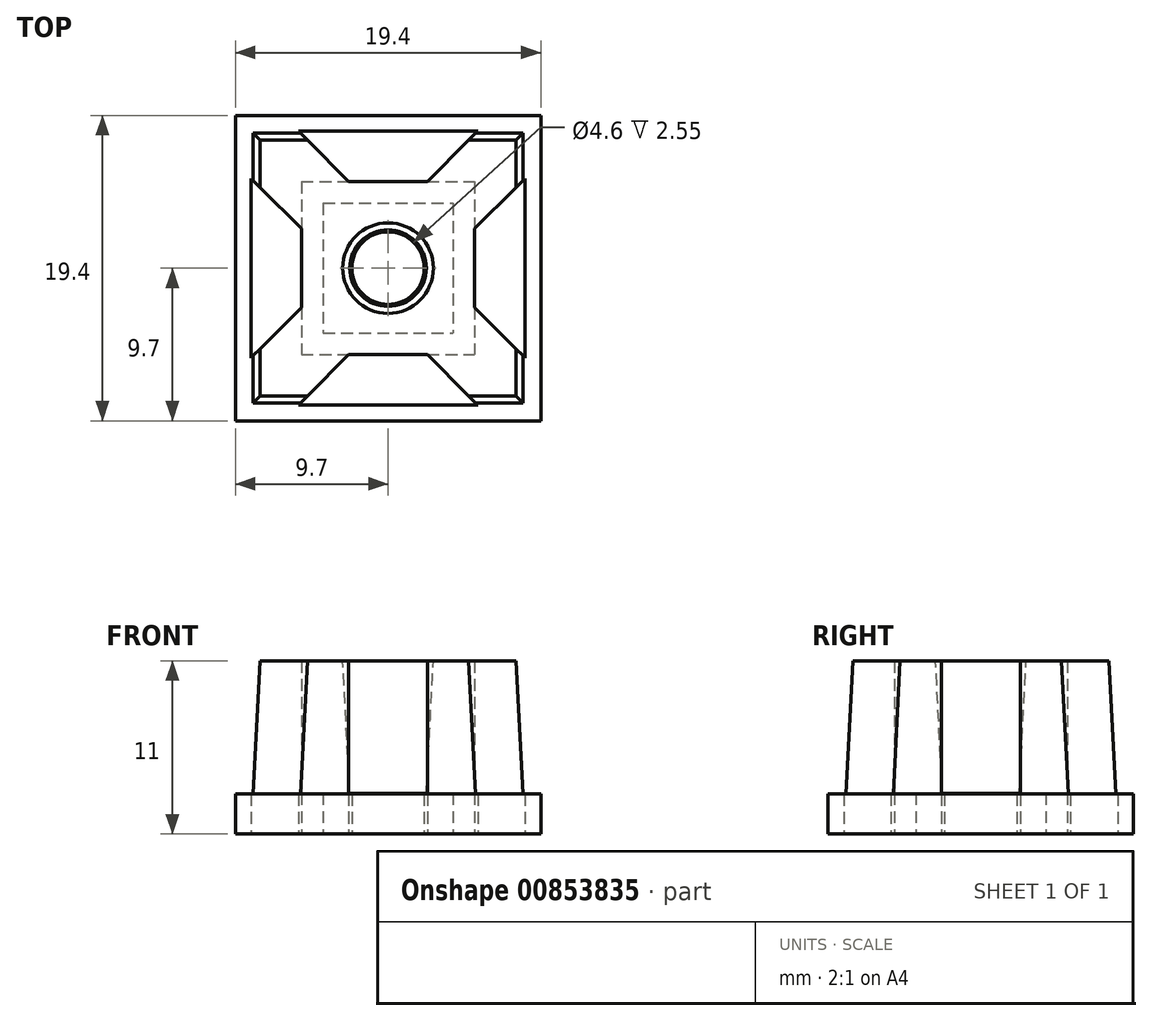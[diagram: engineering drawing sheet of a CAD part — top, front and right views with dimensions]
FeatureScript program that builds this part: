
annotation { "Feature Type Name" : "Feature", "Feature Type Description" : "" }
export const myFeature = defineFeature(function(context is Context, id is Id, definition is map)
    precondition{}
    {
        {
            var Q0;
            Q0=qCreatedBy(makeId("Top.planeOp"),FACE);
            var sketch = newSketch(context, id + "F0", { "sketchPlane" : qUnion([Q0])});
            skLineSegment(sketch, "E0.bottom", {"start": v(-9.7, 9.7) * mm, "end": v(9.7, 9.7) * mm});
            skLineSegment(sketch, "E0.top", {"start": v(-9.7, -9.7) * mm, "end": v(9.7, -9.7) * mm});
            skLineSegment(sketch, "E0.left", {"start": v(-9.7, 9.7) * mm, "end": v(-9.7, -9.7) * mm});
            skLineSegment(sketch, "E0.right", {"start": v(9.7, 9.7) * mm, "end": v(9.7, -9.7) * mm});
            skPoint(sketch, "E0.middle", {"position": v(0, 0) * mm});
            skLineSegment(sketch, "E1.bottom", {"start": v(-8.7, 8.7) * mm, "end": v(-7.95, 8.7) * mm});
            skLineSegment(sketch, "E1.top", {"start": v(-8.7, -8.7) * mm, "end": v(-7.95, -8.7) * mm});
            skLineSegment(sketch, "E1.left", {"start": v(-8.7, 8.7) * mm, "end": v(-8.7, 7.95) * mm});
            skLineSegment(sketch, "E1.right", {"start": v(8.7, 8.7) * mm, "end": v(8.7, 7.95) * mm});
            skArc(sketch, "E2", {"start": v(-7.45, 8.7) * mm, "mid": v(-7.7, 8.95) * mm, "end": v(-7.95, 8.7) * mm});
            skArc(sketch, "E3", {"start": v(-8.7, 7.95) * mm, "mid": v(-8.95, 7.7) * mm, "end": v(-8.7, 7.45) * mm});
            skArc(sketch, "E4", {"start": v(-8.7, -7.45) * mm, "mid": v(-8.95, -7.7) * mm, "end": v(-8.7, -7.95) * mm});
            skArc(sketch, "E5", {"start": v(-7.95, -8.7) * mm, "mid": v(-7.7, -8.95) * mm, "end": v(-7.45, -8.7) * mm});
            skArc(sketch, "E6", {"start": v(7.45, -8.7) * mm, "mid": v(7.7, -8.95) * mm, "end": v(7.95, -8.7) * mm});
            skArc(sketch, "E7", {"start": v(8.7, -7.95) * mm, "mid": v(8.95, -7.7) * mm, "end": v(8.7, -7.45) * mm});
            skArc(sketch, "E8", {"start": v(8.7, 7.45) * mm, "mid": v(8.95, 7.7) * mm, "end": v(8.7, 7.95) * mm});
            skArc(sketch, "E9", {"start": v(7.95, 8.7) * mm, "mid": v(7.7, 8.95) * mm, "end": v(7.45, 8.7) * mm});
            skCircle(sketch, "E10", {"center": v(0, 0) * mm, "radius": 2.3 * mm});
            skLineSegment(sketch, "E11.bottom", {"start": v(-4.12, 4.12) * mm, "end": v(4.12, 4.12) * mm});
            skLineSegment(sketch, "E11.top", {"start": v(-4.13, -4.12) * mm, "end": v(4.12, -4.12) * mm});
            skLineSegment(sketch, "E11.left", {"start": v(-4.12, 4.12) * mm, "end": v(-4.13, -4.12) * mm});
            skLineSegment(sketch, "E11.right", {"start": v(4.13, 4.12) * mm, "end": v(4.12, -4.12) * mm});
            skLineSegment(sketch, "E12", {"start": v(-5.7, -8.7) * mm, "end": v(-2.5, -5.5) * mm});
            skLineSegment(sketch, "E13", {"start": v(-8.7, -5.7) * mm, "end": v(-5.5, -2.5) * mm});
            skLineSegment(sketch, "E14", {"start": v(-8.7, 5.7) * mm, "end": v(-5.5, 2.5) * mm});
            skLineSegment(sketch, "E15", {"start": v(-5.7, 8.7) * mm, "end": v(-2.5, 5.5) * mm});
            skLineSegment(sketch, "E16", {"start": v(5.7, 8.7) * mm, "end": v(2.5, 5.5) * mm});
            skLineSegment(sketch, "E17", {"start": v(8.7, 5.7) * mm, "end": v(5.5, 2.5) * mm});
            skLineSegment(sketch, "E18", {"start": v(5.5, -2.5) * mm, "end": v(8.7, -5.7) * mm});
            skLineSegment(sketch, "E19", {"start": v(2.5, -5.5) * mm, "end": v(5.7, -8.7) * mm});
            skLineSegment(sketch, "E20.bottom", {"start": v(-5.5, 5.5) * mm, "end": v(5.5, 5.5) * mm});
            skLineSegment(sketch, "E20.top", {"start": v(-5.5, -5.5) * mm, "end": v(5.5, -5.5) * mm});
            skLineSegment(sketch, "E20.left", {"start": v(-5.5, 5.5) * mm, "end": v(-5.5, -5.5) * mm});
            skLineSegment(sketch, "E20.right", {"start": v(5.5, 5.5) * mm, "end": v(5.5, -5.5) * mm});
            skLineSegment(sketch, "E21.trimOffspring", {"start": v(-7.45, 8.7) * mm, "end": v(7.45, 8.7) * mm});
            skLineSegment(sketch, "E22.trimOffspring", {"start": v(-8.7, 7.45) * mm, "end": v(-8.7, -7.45) * mm});
            skLineSegment(sketch, "E23.trimOffspring", {"start": v(7.95, 8.7) * mm, "end": v(8.7, 8.7) * mm});
            skLineSegment(sketch, "E24.trimOffspring", {"start": v(8.7, 7.45) * mm, "end": v(8.7, -7.45) * mm});
            skLineSegment(sketch, "E25.trimOffspring", {"start": v(7.95, -8.7) * mm, "end": v(8.7, -8.7) * mm});
            skLineSegment(sketch, "E26.trimOffspring", {"start": v(8.7, -7.95) * mm, "end": v(8.7, -8.7) * mm});
            skLineSegment(sketch, "E27.trimOffspring", {"start": v(-8.7, -7.95) * mm, "end": v(-8.7, -8.7) * mm});
            skLineSegment(sketch, "E28.trimOffspring", {"start": v(-7.45, -8.7) * mm, "end": v(7.45, -8.7) * mm});
            skLineSegment(sketch, "E29", {"start": v(7.95, 8.7) * mm, "end": v(7.45, 8.7) * mm});
            skLineSegment(sketch, "E30", {"start": v(8.7, 7.95) * mm, "end": v(8.7, 7.45) * mm});
            skLineSegment(sketch, "E31", {"start": v(8.7, -7.45) * mm, "end": v(8.7, -7.95) * mm});
            skLineSegment(sketch, "E32", {"start": v(7.95, -8.7) * mm, "end": v(7.45, -8.7) * mm});
            skLineSegment(sketch, "E33", {"start": v(-7.45, -8.7) * mm, "end": v(-7.95, -8.7) * mm});
            skLineSegment(sketch, "E34", {"start": v(-8.7, -7.45) * mm, "end": v(-8.7, -7.95) * mm});
            skLineSegment(sketch, "E35", {"start": v(-8.7, 7.95) * mm, "end": v(-8.7, 7.45) * mm});
            skLineSegment(sketch, "E36", {"start": v(-7.95, 8.7) * mm, "end": v(-7.45, 8.7) * mm});
            skSolve(sketch);
        }
        {
            var Q0;
            Q0=makeQuery(id+"F0.imprint","IMPRINT",FACE,{"disambiguationData":[TD([[makeQuery(id+"F0.imprint","IMPRINT",EDGE,{"derivedFrom":sQuery(id+"F0.wireOp",EDGE,"E0.bottom")}),-1.0]])]});
            extrude(context, id + "F1", {"entities" : qUnion([Q0]), "depth" : 2.54 * mm, "offsetDistance" : 25 * mm});
        }
        {
            var Q0;
            Q0=makeQuery(id+"F0.imprint","IMPRINT",FACE,{"disambiguationData":[TD([[makeQuery(id+"F0.imprint","IMPRINT",EDGE,{"derivedFrom":sQuery(id+"F0.wireOp",EDGE,"E6")}),1.0]])]});
            var Q1;
            {var subQ1=sQuery(id+"F0.wireOp",EDGE,"E18");Q1=makeQuery(id+"F0.imprint","IMPRINT",FACE,{"disambiguationData":[TD([[makeQuery(id+"F0.imprint","IMPRINT",EDGE,{"derivedFrom":subQ1}),-1.0]])]});}
            var Q2;
            Q2=makeQuery(id+"F0.imprint","IMPRINT",FACE,{"disambiguationData":[TD([[makeQuery(id+"F0.imprint","IMPRINT",EDGE,{"derivedFrom":sQuery(id+"F0.wireOp",EDGE,"E9")}),1.0]])]});
            var Q3;
            Q3=makeQuery(id+"F0.imprint","IMPRINT",FACE,{"disambiguationData":[TD([[makeQuery(id+"F0.imprint","IMPRINT",EDGE,{"derivedFrom":sQuery(id+"F0.wireOp",EDGE,"E1.right")}),-1.0]])]});
            var Q4;
            Q4=makeQuery(id+"F0.imprint","IMPRINT",FACE,{"disambiguationData":[TD([[makeQuery(id+"F0.imprint","IMPRINT",EDGE,{"derivedFrom":sQuery(id+"F0.wireOp",EDGE,"E8")}),1.0]])]});
            var Q5;
            Q5=makeQuery(id+"F0.imprint","IMPRINT",FACE,{"disambiguationData":[TD([[makeQuery(id+"F0.imprint","IMPRINT",EDGE,{"derivedFrom":sQuery(id+"F0.wireOp",EDGE,"E11.bottom")}),1.0]])]});
            var Q6;
            Q6=makeQuery(id+"F0.imprint","IMPRINT",FACE,{"disambiguationData":[TD([[makeQuery(id+"F0.imprint","IMPRINT",EDGE,{"derivedFrom":sQuery(id+"F0.wireOp",EDGE,"E10")}),-1.0]])]});
            var Q7;
            {var subQ0=sQuery(id+"F0.wireOp",EDGE,"E17");Q7=makeQuery(id+"F0.imprint","IMPRINT",FACE,{"disambiguationData":[TD([[makeQuery(id+"F0.imprint","IMPRINT",EDGE,{"derivedFrom":subQ0}),1.0]])]});}
            var Q8;
            {var subQ0=sQuery(id+"F0.wireOp",EDGE,"E15");Q8=makeQuery(id+"F0.imprint","IMPRINT",FACE,{"disambiguationData":[TD([[makeQuery(id+"F0.imprint","IMPRINT",EDGE,{"derivedFrom":subQ0}),1.0]])]});}
            var Q9;
            Q9=makeQuery(id+"F0.imprint","IMPRINT",FACE,{"disambiguationData":[TD([[makeQuery(id+"F0.imprint","IMPRINT",EDGE,{"derivedFrom":sQuery(id+"F0.wireOp",EDGE,"E7")}),1.0]])]});
            var Q10;
            {var subQ0=sQuery(id+"F0.wireOp",EDGE,"E12");Q10=makeQuery(id+"F0.imprint","IMPRINT",FACE,{"disambiguationData":[TD([[makeQuery(id+"F0.imprint","IMPRINT",EDGE,{"derivedFrom":subQ0}),-1.0]])]});}
            var Q11;
            Q11=makeQuery(id+"F0.imprint","IMPRINT",FACE,{"disambiguationData":[TD([[makeQuery(id+"F0.imprint","IMPRINT",EDGE,{"derivedFrom":sQuery(id+"F0.wireOp",EDGE,"E1.top")}),1.0]])]});
            var Q12;
            Q12=makeQuery(id+"F0.imprint","IMPRINT",FACE,{"disambiguationData":[TD([[makeQuery(id+"F0.imprint","IMPRINT",EDGE,{"derivedFrom":sQuery(id+"F0.wireOp",EDGE,"E4")}),1.0]])]});
            var Q13;
            Q13=makeQuery(id+"F0.imprint","IMPRINT",FACE,{"disambiguationData":[TD([[makeQuery(id+"F0.imprint","IMPRINT",EDGE,{"derivedFrom":sQuery(id+"F0.wireOp",EDGE,"E5")}),1.0]])]});
            var Q14;
            {var subQ0=sQuery(id+"F0.wireOp",EDGE,"E13");Q14=makeQuery(id+"F0.imprint","IMPRINT",FACE,{"disambiguationData":[TD([[makeQuery(id+"F0.imprint","IMPRINT",EDGE,{"derivedFrom":subQ0}),1.0]])]});}
            var Q15;
            Q15=makeQuery(id+"F0.imprint","IMPRINT",FACE,{"disambiguationData":[TD([[makeQuery(id+"F0.imprint","IMPRINT",EDGE,{"derivedFrom":sQuery(id+"F0.wireOp",EDGE,"E1.bottom")}),-1.0]])]});
            var Q16;
            Q16=makeQuery(id+"F0.imprint","IMPRINT",FACE,{"disambiguationData":[TD([[makeQuery(id+"F0.imprint","IMPRINT",EDGE,{"derivedFrom":sQuery(id+"F0.wireOp",EDGE,"E3")}),1.0]])]});
            var Q17;
            Q17=makeQuery(id+"F0.imprint","IMPRINT",FACE,{"disambiguationData":[TD([[makeQuery(id+"F0.imprint","IMPRINT",EDGE,{"derivedFrom":sQuery(id+"F0.wireOp",EDGE,"E2")}),1.0]])]});
            extrude(context, id + "F2", {"entities" : qUnion([Q0, Q1, Q2, Q3, Q4, Q5, Q6, Q7, Q8, Q9, Q10, Q11, Q12, Q13, Q14, Q15, Q16, Q17]), "operationType" : NewBodyOperationType.ADD, "depth" : 2.55 * mm, "offsetDistance" : 25 * mm});
        }
        {
            var Q0;
            Q0=makeQuery(id+"F0.imprint","IMPRINT",FACE,{"disambiguationData":[TD([[makeQuery(id+"F0.imprint","IMPRINT",EDGE,{"derivedFrom":sQuery(id+"F0.wireOp",EDGE,"E1.bottom")}),-1.0]])]});
            var Q1;
            {var subQ0=sQuery(id+"F0.wireOp",EDGE,"E15");Q1=makeQuery(id+"F0.imprint","IMPRINT",FACE,{"disambiguationData":[TD([[makeQuery(id+"F0.imprint","IMPRINT",EDGE,{"derivedFrom":subQ0}),1.0]])]});}
            var Q2;
            Q2=makeQuery(id+"F0.imprint","IMPRINT",FACE,{"disambiguationData":[TD([[makeQuery(id+"F0.imprint","IMPRINT",EDGE,{"derivedFrom":sQuery(id+"F0.wireOp",EDGE,"E1.right")}),-1.0]])]});
            var Q3;
            {var subQ0=sQuery(id+"F0.wireOp",EDGE,"E17");Q3=makeQuery(id+"F0.imprint","IMPRINT",FACE,{"disambiguationData":[TD([[makeQuery(id+"F0.imprint","IMPRINT",EDGE,{"derivedFrom":subQ0}),1.0]])]});}
            var Q4;
            {var subQ1=sQuery(id+"F0.wireOp",EDGE,"E18");Q4=makeQuery(id+"F0.imprint","IMPRINT",FACE,{"disambiguationData":[TD([[makeQuery(id+"F0.imprint","IMPRINT",EDGE,{"derivedFrom":subQ1}),-1.0]])]});}
            var Q5;
            {var subQ0=sQuery(id+"F0.wireOp",EDGE,"E12");Q5=makeQuery(id+"F0.imprint","IMPRINT",FACE,{"disambiguationData":[TD([[makeQuery(id+"F0.imprint","IMPRINT",EDGE,{"derivedFrom":subQ0}),-1.0]])]});}
            var Q6;
            Q6=makeQuery(id+"F0.imprint","IMPRINT",FACE,{"disambiguationData":[TD([[makeQuery(id+"F0.imprint","IMPRINT",EDGE,{"derivedFrom":sQuery(id+"F0.wireOp",EDGE,"E1.top")}),1.0]])]});
            var Q7;
            {var subQ0=sQuery(id+"F0.wireOp",EDGE,"E13");Q7=makeQuery(id+"F0.imprint","IMPRINT",FACE,{"disambiguationData":[TD([[makeQuery(id+"F0.imprint","IMPRINT",EDGE,{"derivedFrom":subQ0}),1.0]])]});}
            var Q8;
            Q8=makeQuery(id+"F0.imprint","IMPRINT",FACE,{"disambiguationData":[TD([[makeQuery(id+"F0.imprint","IMPRINT",EDGE,{"derivedFrom":sQuery(id+"F0.wireOp",EDGE,"E11.bottom")}),1.0]])]});
            var Q9;
            Q9=makeQuery(id+"F0.imprint","IMPRINT",FACE,{"disambiguationData":[TD([[makeQuery(id+"F0.imprint","IMPRINT",EDGE,{"derivedFrom":sQuery(id+"F0.wireOp",EDGE,"E10")}),-1.0]])]});
            extrude(context, id + "F3", {"entities" : qUnion([Q0, Q1, Q2, Q3, Q4, Q5, Q6, Q7, Q8, Q9]), "operationType" : NewBodyOperationType.ADD, "depth" : 11 * mm, "offsetDistance" : 25 * mm, "hasDraft" : true, "draftAngle" : 3 * degree, "draftPullDirection" : true});
        }
        {
            var Q0;
            {var subQ0=sQuery(id+"F0.wireOp",EDGE,"E13");Q0=makeQuery(id+"F0.imprint","IMPRINT",FACE,{"disambiguationData":[TD([[makeQuery(id+"F0.imprint","IMPRINT",EDGE,{"derivedFrom":subQ0}),1.0]])]});}
            var Q1;
            {var subQ0=sQuery(id+"F0.wireOp",EDGE,"E15");Q1=makeQuery(id+"F0.imprint","IMPRINT",FACE,{"disambiguationData":[TD([[makeQuery(id+"F0.imprint","IMPRINT",EDGE,{"derivedFrom":subQ0}),1.0]])]});}
            var Q2;
            {var subQ0=sQuery(id+"F0.wireOp",EDGE,"E17");Q2=makeQuery(id+"F0.imprint","IMPRINT",FACE,{"disambiguationData":[TD([[makeQuery(id+"F0.imprint","IMPRINT",EDGE,{"derivedFrom":subQ0}),1.0]])]});}
            var Q3;
            {var subQ0=sQuery(id+"F0.wireOp",EDGE,"E12");Q3=makeQuery(id+"F0.imprint","IMPRINT",FACE,{"disambiguationData":[TD([[makeQuery(id+"F0.imprint","IMPRINT",EDGE,{"derivedFrom":subQ0}),-1.0]])]});}
            extrude(context, id + "F4", {"entities" : qUnion([Q0, Q1, Q2, Q3]), "operationType" : NewBodyOperationType.REMOVE, "depth" : 11 * mm, "offsetDistance" : 25 * mm});
        }
        {
            var Q0;
            Q0=makeQuery(id+"F0.imprint","IMPRINT",FACE,{"disambiguationData":[TD([[makeQuery(id+"F0.imprint","IMPRINT",EDGE,{"derivedFrom":sQuery(id+"F0.wireOp",EDGE,"E11.bottom")}),1.0]])]});
            extrude(context, id + "F5", {"entities" : qUnion([Q0]), "operationType" : NewBodyOperationType.REMOVE, "depth" : 2.6 * mm, "offsetDistance" : 25 * mm});
        }
    });
